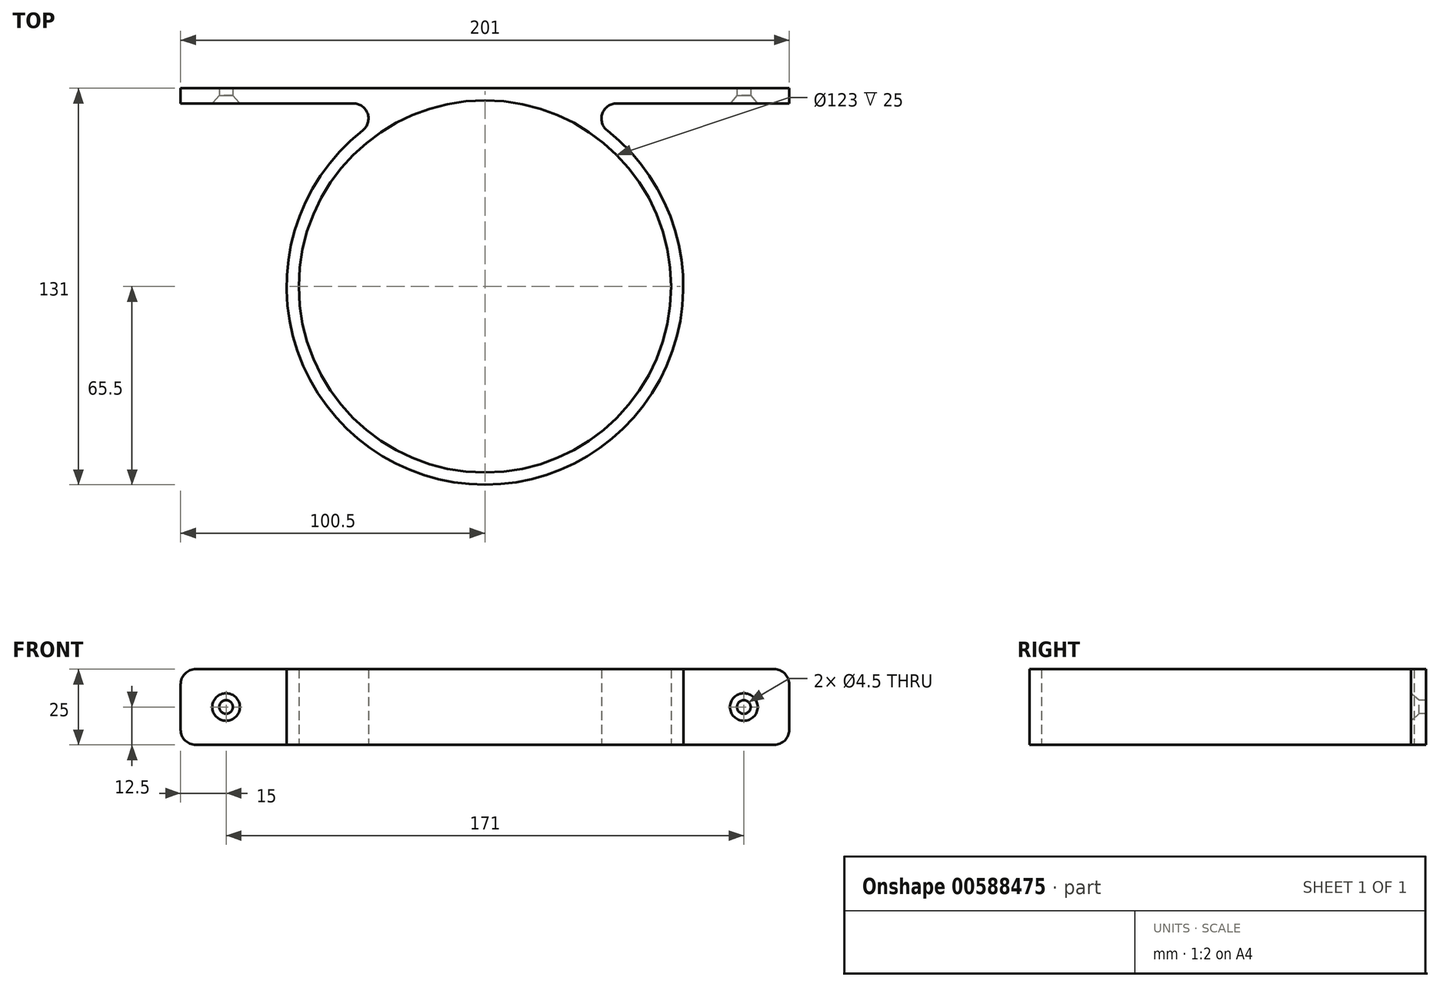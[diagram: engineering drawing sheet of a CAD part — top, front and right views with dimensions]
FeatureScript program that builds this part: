
annotation { "Feature Type Name" : "Feature", "Feature Type Description" : "" }
export const myFeature = defineFeature(function(context is Context, id is Id, definition is map)
    precondition{}
    {
        {
            var Q0;
            Q0=qCreatedBy(makeId("Top.planeOp"),FACE);
            var sketch = newSketch(context, id + "F0", { "sketchPlane" : qUnion([Q0])});
            skLineSegment(sketch, "E0.bottom", {"start": v(-100.5, 2.5) * mm, "end": v(100.5, 2.5) * mm});
            skLineSegment(sketch, "E0.top", {"start": v(-100.5, -2.5) * mm, "end": v(100.5, -2.5) * mm});
            skLineSegment(sketch, "E0.left", {"start": v(-100.5, 2.5) * mm, "end": v(-100.5, -2.5) * mm});
            skLineSegment(sketch, "E0.right", {"start": v(100.5, 2.5) * mm, "end": v(100.5, -2.5) * mm});
            skPoint(sketch, "E0.middle", {"position": v(0, 0) * mm});
            skCircle(sketch, "E1", {"center": v(0, -63) * mm, "radius": 65.5 * mm});
            skCircle(sketch, "E2", {"center": v(0, -63) * mm, "radius": 61.5 * mm});
            skSolve(sketch);
        }
        {
            var Q0;
            {var subQ0=sQuery(id+"F0.wireOp",EDGE,"E1");var subQ1=sQuery(id+"F0.wireOp",EDGE,"E0.top");var subQ2=makeQuery(id+"F0.imprint","INTERSECT",VERTEX,{"disambiguationData":[OD(0.0)],"derivedFrom":[subQ1,subQ0]});Q0=makeQuery(id+"F0.imprint","IMPRINT",FACE,{"disambiguationData":[TD([[makeQuery(id+"F0.imprint","IMPRINT",EDGE,{"disambiguationData":[TD([[subQ2,-1.0]])],"derivedFrom":subQ1}),-1.0]])]});}
            var Q1;
            {var subQ0=sQuery(id+"F0.wireOp",EDGE,"E0.left");Q1=makeQuery(id+"F0.imprint","IMPRINT",FACE,{"disambiguationData":[TD([[makeQuery(id+"F0.imprint","IMPRINT",EDGE,{"derivedFrom":subQ0}),1.0]])]});}
            var Q2;
            {var subQ0=sQuery(id+"F0.wireOp",EDGE,"E1");var subQ2=sQuery(id+"F0.wireOp",EDGE,"E0.top");var subQ4=makeQuery(id+"F0.imprint","INTERSECT",VERTEX,{"disambiguationData":[OD(0.0)],"derivedFrom":[subQ2,subQ0]});Q2=makeQuery(id+"F0.imprint","IMPRINT",FACE,{"disambiguationData":[TD([[makeQuery(id+"F0.imprint","IMPRINT",EDGE,{"disambiguationData":[TD([[subQ4,-1.0]])],"derivedFrom":subQ2}),1.0]])]});}
            var Q3;
            {var subQ0=sQuery(id+"F0.wireOp",EDGE,"E0.right");Q3=makeQuery(id+"F0.imprint","IMPRINT",FACE,{"disambiguationData":[TD([[makeQuery(id+"F0.imprint","IMPRINT",EDGE,{"derivedFrom":subQ0}),-1.0]])]});}
            extrude(context, id + "F1", {"entities" : qUnion([Q0, Q1, Q2, Q3]), "depth" : 25 * mm, "offsetDistance" : 25 * mm});
        }
        {
            var Q0;
            {var subQ0=sQuery(id+"F0.wireOp",EDGE,"E1");var subQ1=sQuery(id+"F0.wireOp",EDGE,"E0.top");Q0=makeQuery(id+"F1.opExtrude","SWEPT_EDGE",EDGE,{"disambiguationData":[OSD([subQ1,subQ0]),TDD([makeQuery(id+"F0.imprint","INTERSECT",VERTEX,{"disambiguationData":[OD(0.0)],"derivedFrom":[subQ1,subQ0]})])]});}
            var Q1;
            {var subQ0=sQuery(id+"F0.wireOp",EDGE,"E1");var subQ1=sQuery(id+"F0.wireOp",EDGE,"E0.top");Q1=makeQuery(id+"F1.opExtrude","SWEPT_EDGE",EDGE,{"disambiguationData":[OSD([subQ1,subQ0]),TDD([makeQuery(id+"F0.imprint","INTERSECT",VERTEX,{"disambiguationData":[OD(1.0)],"derivedFrom":[subQ1,subQ0]})])]});}
            fillet(context, id + "F2", {"entities" : qUnion([Q0, Q1]), "radius" : 5 * mm, "tangentPropagation" : true, "allowEdgeOverflow" : false});
        }
        {
            var Q0;
            Q0=makeQuery(id+"F1.opExtrude","CAP_EDGE",EDGE,{"disambiguationData":[OSD([sQuery(id+"F0.wireOp",EDGE,"E0.left")])],"isStart":false});
            var Q1;
            Q1=makeQuery(id+"F1.opExtrude","CAP_EDGE",EDGE,{"disambiguationData":[OSD([sQuery(id+"F0.wireOp",EDGE,"E0.left")])],"isStart":true});
            var Q2;
            Q2=makeQuery(id+"F1.opExtrude","CAP_EDGE",EDGE,{"disambiguationData":[OSD([sQuery(id+"F0.wireOp",EDGE,"E0.right")])],"isStart":false});
            var Q3;
            Q3=makeQuery(id+"F1.opExtrude","CAP_EDGE",EDGE,{"disambiguationData":[OSD([sQuery(id+"F0.wireOp",EDGE,"E0.right")])],"isStart":true});
            fillet(context, id + "F3", {"entities" : qUnion([Q0, Q1, Q2, Q3]), "radius" : 5 * mm, "tangentPropagation" : true, "allowEdgeOverflow" : false});
        }
        {
            var Q0;
            {var subQ0=sQuery(id+"F0.wireOp",EDGE,"E0.top");Q0=makeQuery(id+"F1.opExtrude","SWEPT_FACE",FACE,{"disambiguationData":[OSD([subQ0]),TDD([makeQuery(id+"F0.imprint","IMPRINT",EDGE,{"disambiguationData":[TD([[makeQuery(id+"F0.imprint","INTERSECT",VERTEX,{"derivedFrom":[subQ0,sQuery(id+"F0.wireOp",EDGE,"E0.right")]}),1.0]])],"derivedFrom":subQ0})])]});}
            var sketch = newSketch(context, id + "F4", { "sketchPlane" : qUnion([Q0])});
            skLineSegment(sketch, "E3", {"start": v(-85.5, 12.5) * mm, "end": v(85.5, 12.5) * mm, "construction": true});
            skLineSegment(sketch, "E4", {"start": v(0, 0) * mm, "end": v(0, 12.5) * mm, "construction": true});
            skLineSegment(sketch, "E5", {"start": v(0, 12.5) * mm, "end": v(0, 25) * mm, "construction": true});
            skSolve(sketch);
        }
        {
            var Q0;
            Q0=sQuery(id+"F4.wireOp",VERTEX,"E3.start");
            var Q1;
            Q1=sQuery(id+"F4.wireOp",VERTEX,"E3.end");
            var Q2;
            Q2=makeQuery(id+"F1.opExtrude","SWEPT_BODY",BODY,{"disambiguationData":[OSD([sQuery(id+"F0.wireOp",EDGE,"E0.bottom"),sQuery(id+"F0.wireOp",EDGE,"E0.top"),sQuery(id+"F0.wireOp",EDGE,"E0.left"),sQuery(id+"F0.wireOp",EDGE,"E0.right"),sQuery(id+"F0.wireOp",EDGE,"E1"),sQuery(id+"F0.wireOp",EDGE,"E2")])]});
            hole(context, id + "F5", {"style" : HoleStyle.C_SINK, "endStyle" : HoleEndStyle.BLIND, "standardTappedOrClearance" : lookupTablePath({ "standard" : "ANSI", "fit" : "Normal (ASME)", "size" : "#8", "type" : "Clearance" }), "standardBlindInLast" : lookupTablePath({ "fit" : "Free", "standard" : "ANSI", "size" : "#8", "type" : "Clearance" }), "holeDiameter" : 4.5 * mm, "cSinkDiameter" : 9.12 * mm, "cSinkAngle" : 82 * degree, "majorDiameter" : 5 * mm, "holeDepth" : 5 * mm, "isTappedThrough" : true, "tappedDepth" : 3.5 * mm, "tapClearance" : 3, "locations" : qUnion([Q0, Q1]), "scope" : qUnion([Q2])});
        }
    });
